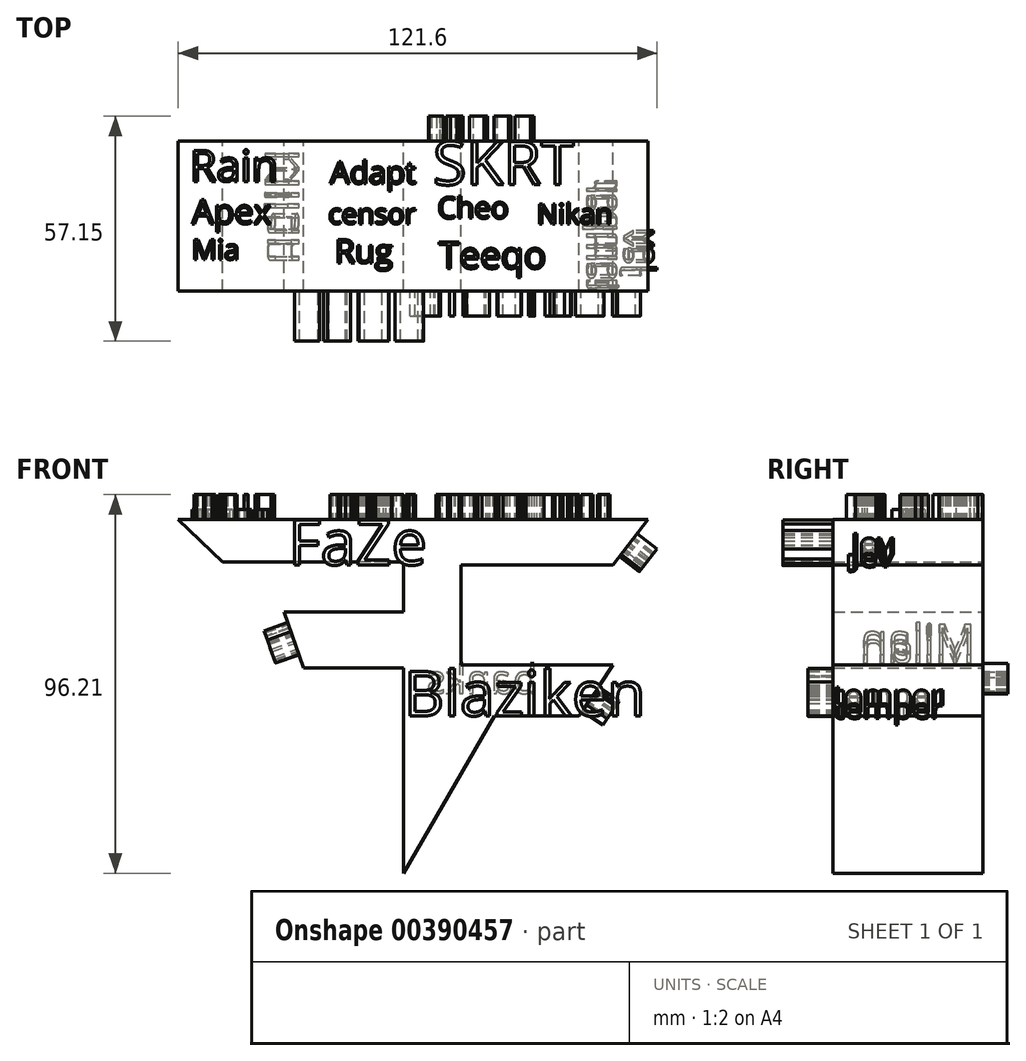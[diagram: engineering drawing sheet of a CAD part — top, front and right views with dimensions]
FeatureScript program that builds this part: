
annotation { "Feature Type Name" : "Feature", "Feature Type Description" : "" }
export const myFeature = defineFeature(function(context is Context, id is Id, definition is map)
    precondition{}
    {
        {
            var Q0;
            Q0=qCreatedBy(makeId("Front.planeOp"),FACE);
            var sketch = newSketch(context, id + "F0", { "sketchPlane" : qUnion([Q0])});
            skLineSegment(sketch, "E0", {"start": v(-52.84, 49.84) * mm, "end": v(58.59, 49.84) * mm});
            skLineSegment(sketch, "E1", {"start": v(58.59, 49.84) * mm, "end": v(49.72, 38.34) * mm});
            skLineSegment(sketch, "E2", {"start": v(49.72, 38.34) * mm, "end": v(11.14, 38.34) * mm});
            skLineSegment(sketch, "E3", {"start": v(11.14, 38.34) * mm, "end": v(11.14, 12.94) * mm});
            skLineSegment(sketch, "E4", {"start": v(11.14, 12.94) * mm, "end": v(49.72, 12.94) * mm});
            skLineSegment(sketch, "E5", {"start": v(49.72, 12.94) * mm, "end": v(41.1, 0) * mm});
            skLineSegment(sketch, "E6", {"start": v(41.1, 0) * mm, "end": v(19.53, 0) * mm});
            skLineSegment(sketch, "E7", {"start": v(19.53, 0) * mm, "end": v(-3.47, -40.02) * mm});
            skLineSegment(sketch, "E8", {"start": v(-3.47, -40.02) * mm, "end": v(-3.47, 12.22) * mm});
            skLineSegment(sketch, "E9", {"start": v(-3.47, 12.22) * mm, "end": v(-28.87, 12.22) * mm});
            skLineSegment(sketch, "E10", {"start": v(-28.87, 12.22) * mm, "end": v(-33.9, 26.36) * mm});
            skLineSegment(sketch, "E11", {"start": v(-33.9, 26.36) * mm, "end": v(-3.47, 26.36) * mm});
            skLineSegment(sketch, "E12", {"start": v(-3.47, 26.36) * mm, "end": v(-3.47, 39.06) * mm});
            skLineSegment(sketch, "E13", {"start": v(-3.47, 39.06) * mm, "end": v(-49.48, 39.06) * mm});
            skLineSegment(sketch, "E14", {"start": v(-49.48, 39.06) * mm, "end": v(-60.74, 49.84) * mm});
            skLineSegment(sketch, "E15", {"start": v(-60.74, 49.84) * mm, "end": v(-52.84, 49.84) * mm});
            skSolve(sketch);
        }
        {
            var Q0;
            Q0 = qSketchRegion(id + "F0", true);
            extrude(context, id + "F1", {"entities" : qUnion([Q0]), "depth" : 38.1 * mm});
        }
        {
            var Q0;
            Q0 = qSketchRegion(id + "F0", true);
            extrude(context, id + "F2", {"entities" : qUnion([Q0]), "operationType" : NewBodyOperationType.ADD, "depth" : 25.4 * mm});
        }
        {
            var Q0;
            Q0=makeQuery(id+"F1.opExtrude","CAP_FACE",FACE,{"disambiguationData":[OSD([sQuery(id+"F0.wireOp",EDGE,"E0"),sQuery(id+"F0.wireOp",EDGE,"E1"),sQuery(id+"F0.wireOp",EDGE,"E2"),sQuery(id+"F0.wireOp",EDGE,"E3"),sQuery(id+"F0.wireOp",EDGE,"E4"),sQuery(id+"F0.wireOp",EDGE,"E5"),sQuery(id+"F0.wireOp",EDGE,"E6"),sQuery(id+"F0.wireOp",EDGE,"E7"),sQuery(id+"F0.wireOp",EDGE,"E8"),sQuery(id+"F0.wireOp",EDGE,"E9"),sQuery(id+"F0.wireOp",EDGE,"E10"),sQuery(id+"F0.wireOp",EDGE,"E11"),sQuery(id+"F0.wireOp",EDGE,"E12"),sQuery(id+"F0.wireOp",EDGE,"E13"),sQuery(id+"F0.wireOp",EDGE,"E14"),sQuery(id+"F0.wireOp",EDGE,"E15")])],"isStart":false});
            var sketch = newSketch(context, id + "F3", { "sketchPlane" : qUnion([Q0])});
            skText(sketch, "E16", { "text": "FaZe", "fontName": "OpenSans-Regular.ttf"});
            const initialGuessF3  = {"E16": [-0.03281, 0.03834, 1, 0, 0.0115]};
            skSetInitialGuess(sketch, initialGuessF3);
            skSolve(sketch);
        }
        {
            var Q0;
            Q0 = qSketchRegion(id + "F3", true);
            extrude(context, id + "F4", {"entities" : qUnion([Q0]), "operationType" : NewBodyOperationType.ADD, "depth" : 12.7 * mm});
        }
        {
            var Q0;
            Q0=makeQuery(id+"F1.opExtrude","SWEPT_FACE",FACE,{"disambiguationData":[OSD([sQuery(id+"F0.wireOp",EDGE,"E0"),sQuery(id+"F0.wireOp",EDGE,"E15")])]});
            var sketch = newSketch(context, id + "F5", { "sketchPlane" : qUnion([Q0])});
            skText(sketch, "E17", { "text": "Rain", "fontName": "OpenSans-Regular.ttf"});
            const initialGuessF5  = {"E17": [-0.05788, -0.01021, 1, 0, 0.00794]};
            skSetInitialGuess(sketch, initialGuessF5);
            skSolve(sketch);
        }
        {
            var Q0;
            Q0 = qSketchRegion(id + "F5", true);
            extrude(context, id + "F6", {"entities" : qUnion([Q0]), "operationType" : NewBodyOperationType.ADD, "depth" : 6.35 * mm});
        }
        {
            var Q0;
            {var subQ0=sQuery(id+"F0.wireOp",EDGE,"E1");var subQ1=sQuery(id+"F0.wireOp",EDGE,"E15");var subQ15=sQuery(id+"F0.wireOp",EDGE,"E0");Q0=makeQuery(id+"F6.boolean.opBoolean","SPLIT",FACE,{"disambiguationData":[TD([makeQuery(id+"F1.opExtrude","SWEPT_FACE",FACE,{"disambiguationData":[OSD([subQ0])]})])],"derivedFrom":makeQuery(id+"F1.opExtrude","SWEPT_FACE",FACE,{"disambiguationData":[OSD([subQ15,subQ1])]})});}
            var sketch = newSketch(context, id + "F7", { "sketchPlane" : qUnion([Q0])});
            skText(sketch, "E18", { "text": "Apex", "fontName": "OpenSans-Regular.ttf"});
            const initialGuessF7  = {"E18": [-0.05731, -0.021, 1, 0, 0.00624]};
            skSetInitialGuess(sketch, initialGuessF7);
            skSolve(sketch);
        }
        {
            var Q0;
            Q0 = qSketchRegion(id + "F7", true);
            extrude(context, id + "F8", {"entities" : qUnion([Q0]), "operationType" : NewBodyOperationType.ADD, "depth" : 2.54 * mm});
        }
        {
            var Q0;
            {var subQ52=sQuery(id+"F0.wireOp",EDGE,"E15");var subQ65=sQuery(id+"F0.wireOp",EDGE,"E1");var subQ66=sQuery(id+"F0.wireOp",EDGE,"E0");var subQ72=makeQuery(id+"F1.opExtrude","SWEPT_FACE",FACE,{"disambiguationData":[OSD([subQ65])]});Q0=makeQuery(id+"F8.boolean.opBoolean","SPLIT",FACE,{"disambiguationData":[TD([subQ72])],"derivedFrom":makeQuery(id+"F6.boolean.opBoolean","SPLIT",FACE,{"disambiguationData":[TD([subQ72])],"derivedFrom":makeQuery(id+"F1.opExtrude","SWEPT_FACE",FACE,{"disambiguationData":[OSD([subQ66,subQ52])]})})});}
            var sketch = newSketch(context, id + "F9", { "sketchPlane" : qUnion([Q0])});
            skText(sketch, "E19", { "text": "Adapt", "fontName": "OpenSans-Regular.ttf"});
            const initialGuessF9  = {"E19": [-0.02216, -0.01078, 1, 0, 0.00567]};
            skSetInitialGuess(sketch, initialGuessF9);
            skSolve(sketch);
        }
        {
            var Q0;
            Q0 = qSketchRegion(id + "F9", true);
            extrude(context, id + "F10", {"entities" : qUnion([Q0]), "operationType" : NewBodyOperationType.ADD, "depth" : 6.35 * mm});
        }
        {
            var Q0;
            {var subQ81=sQuery(id+"F0.wireOp",EDGE,"E15");var subQ94=sQuery(id+"F0.wireOp",EDGE,"E1");var subQ95=sQuery(id+"F0.wireOp",EDGE,"E0");var subQ103=makeQuery(id+"F1.opExtrude","SWEPT_FACE",FACE,{"disambiguationData":[OSD([subQ94])]});Q0=makeQuery(id+"F10.boolean.opBoolean","SPLIT",FACE,{"disambiguationData":[TD([subQ103])],"derivedFrom":makeQuery(id+"F8.boolean.opBoolean","SPLIT",FACE,{"disambiguationData":[TD([subQ103])],"derivedFrom":makeQuery(id+"F6.boolean.opBoolean","SPLIT",FACE,{"disambiguationData":[TD([subQ103])],"derivedFrom":makeQuery(id+"F1.opExtrude","SWEPT_FACE",FACE,{"disambiguationData":[OSD([subQ95,subQ81])]})})})});}
            var sketch = newSketch(context, id + "F11", { "sketchPlane" : qUnion([Q0])});
            skText(sketch, "E20", { "text": "censor", "fontName": "OpenSans-Regular.ttf"});
            const initialGuessF11  = {"E20": [-0.02263, -0.021, 1, 0, 0.0051]};
            skSetInitialGuess(sketch, initialGuessF11);
            skSolve(sketch);
        }
        {
            var Q0;
            Q0 = qSketchRegion(id + "F11", true);
            extrude(context, id + "F12", {"entities" : qUnion([Q0]), "operationType" : NewBodyOperationType.ADD, "depth" : 6.35 * mm});
        }
        {
            var Q0;
            {var subQ25=sQuery(id+"F0.wireOp",EDGE,"E9");var subQ27=sQuery(id+"F0.wireOp",EDGE,"E8");var subQ29=sQuery(id+"F0.wireOp",EDGE,"E7");var subQ31=sQuery(id+"F0.wireOp",EDGE,"E6");var subQ33=sQuery(id+"F0.wireOp",EDGE,"E5");var subQ35=sQuery(id+"F0.wireOp",EDGE,"E4");var subQ37=sQuery(id+"F0.wireOp",EDGE,"E15");var subQ38=sQuery(id+"F0.wireOp",EDGE,"E0");var subQ41=sQuery(id+"F0.wireOp",EDGE,"E1");var subQ43=sQuery(id+"F0.wireOp",EDGE,"E2");var subQ45=sQuery(id+"F0.wireOp",EDGE,"E3");var subQ47=sQuery(id+"F0.wireOp",EDGE,"E10");var subQ49=sQuery(id+"F0.wireOp",EDGE,"E11");var subQ51=sQuery(id+"F0.wireOp",EDGE,"E12");var subQ52=sQuery(id+"F0.wireOp",EDGE,"E13");var subQ53=sQuery(id+"F0.wireOp",EDGE,"E14");Q0=makeQuery(id+"F4.boolean.opBoolean","SPLIT",FACE,{"disambiguationData":[TD([makeQuery(id+"F1.opExtrude","SWEPT_FACE",FACE,{"disambiguationData":[OSD([subQ41])]})])],"derivedFrom":makeQuery(id+"F1.opExtrude","CAP_FACE",FACE,{"disambiguationData":[OSD([subQ38,subQ41,subQ43,subQ45,subQ35,subQ33,subQ31,subQ29,subQ27,subQ25,subQ47,subQ49,subQ51,subQ52,subQ53,subQ37])],"isStart":false})});}
            var sketch = newSketch(context, id + "F13", { "sketchPlane" : qUnion([Q0])});
            skText(sketch, "E21", { "text": "Blaziken", "fontName": "OpenSans-Regular.ttf"});
            skPoint(sketch, "E21.secondSnap0", {"position": v(30.31, 0) * mm});
            const initialGuessF13  = {"E21": [-0.00347, 0, 1, 0, 0.0114]};
            skSetInitialGuess(sketch, initialGuessF13);
            skSolve(sketch);
        }
        {
            var Q0;
            Q0 = qSketchRegion(id + "F13", true);
            extrude(context, id + "F14", {"entities" : qUnion([Q0]), "operationType" : NewBodyOperationType.ADD, "depth" : 6.35 * mm});
        }
        {
            var Q0;
            {var subQ109=sQuery(id+"F0.wireOp",EDGE,"E1");var subQ110=makeQuery(id+"F1.opExtrude","SWEPT_FACE",FACE,{"disambiguationData":[OSD([subQ109])]});var subQ114=sQuery(id+"F0.wireOp",EDGE,"E15");var subQ128=sQuery(id+"F0.wireOp",EDGE,"E0");Q0=makeQuery(id+"F12.boolean.opBoolean","SPLIT",FACE,{"disambiguationData":[TD([subQ110])],"derivedFrom":makeQuery(id+"F10.boolean.opBoolean","SPLIT",FACE,{"disambiguationData":[TD([subQ110])],"derivedFrom":makeQuery(id+"F8.boolean.opBoolean","SPLIT",FACE,{"disambiguationData":[TD([subQ110])],"derivedFrom":makeQuery(id+"F6.boolean.opBoolean","SPLIT",FACE,{"disambiguationData":[TD([subQ110])],"derivedFrom":makeQuery(id+"F1.opExtrude","SWEPT_FACE",FACE,{"disambiguationData":[OSD([subQ128,subQ114])]})})})})});}
            var sketch = newSketch(context, id + "F15", { "sketchPlane" : qUnion([Q0])});
            skText(sketch, "E22", { "text": "SKRT", "fontName": "OpenSans-Regular.ttf"});
            const initialGuessF15  = {"E22": [0.00397, -0.01107, 1, 0, 0.01107]};
            skSetInitialGuess(sketch, initialGuessF15);
            skSolve(sketch);
        }
        {
            var Q0;
            Q0 = qSketchRegion(id + "F15", true);
            extrude(context, id + "F16", {"entities" : qUnion([Q0]), "operationType" : NewBodyOperationType.ADD, "depth" : 6.35 * mm});
        }
        {
            var Q0;
            {var subQ126=sQuery(id+"F0.wireOp",EDGE,"E1");var subQ127=makeQuery(id+"F1.opExtrude","SWEPT_FACE",FACE,{"disambiguationData":[OSD([subQ126])]});var subQ131=sQuery(id+"F0.wireOp",EDGE,"E15");var subQ145=sQuery(id+"F0.wireOp",EDGE,"E0");Q0=makeQuery(id+"F16.boolean.opBoolean","SPLIT",FACE,{"disambiguationData":[TD([subQ127])],"derivedFrom":makeQuery(id+"F12.boolean.opBoolean","SPLIT",FACE,{"disambiguationData":[TD([subQ127])],"derivedFrom":makeQuery(id+"F10.boolean.opBoolean","SPLIT",FACE,{"disambiguationData":[TD([subQ127])],"derivedFrom":makeQuery(id+"F8.boolean.opBoolean","SPLIT",FACE,{"disambiguationData":[TD([subQ127])],"derivedFrom":makeQuery(id+"F6.boolean.opBoolean","SPLIT",FACE,{"disambiguationData":[TD([subQ127])],"derivedFrom":makeQuery(id+"F1.opExtrude","SWEPT_FACE",FACE,{"disambiguationData":[OSD([subQ145,subQ131])]})})})})})});}
            var sketch = newSketch(context, id + "F17", { "sketchPlane" : qUnion([Q0])});
            skText(sketch, "E23", { "text": "Cheo", "fontName": "OpenSans-Regular.ttf"});
            const initialGuessF17  = {"E23": [0.0051, -0.01958, 1, 0, 0.0054]};
            skSetInitialGuess(sketch, initialGuessF17);
            skSolve(sketch);
        }
        {
            var Q0;
            Q0 = qSketchRegion(id + "F17", true);
            extrude(context, id + "F18", {"entities" : qUnion([Q0]), "operationType" : NewBodyOperationType.ADD, "depth" : 6.35 * mm});
        }
        {
            var Q0;
            {var subQ127=sQuery(id+"F0.wireOp",EDGE,"E1");var subQ128=makeQuery(id+"F1.opExtrude","SWEPT_FACE",FACE,{"disambiguationData":[OSD([subQ127])]});var subQ132=sQuery(id+"F0.wireOp",EDGE,"E15");var subQ146=sQuery(id+"F0.wireOp",EDGE,"E0");Q0=makeQuery(id+"F18.boolean.opBoolean","SPLIT",FACE,{"disambiguationData":[TD([subQ128])],"derivedFrom":makeQuery(id+"F16.boolean.opBoolean","SPLIT",FACE,{"disambiguationData":[TD([subQ128])],"derivedFrom":makeQuery(id+"F12.boolean.opBoolean","SPLIT",FACE,{"disambiguationData":[TD([subQ128])],"derivedFrom":makeQuery(id+"F10.boolean.opBoolean","SPLIT",FACE,{"disambiguationData":[TD([subQ128])],"derivedFrom":makeQuery(id+"F8.boolean.opBoolean","SPLIT",FACE,{"disambiguationData":[TD([subQ128])],"derivedFrom":makeQuery(id+"F6.boolean.opBoolean","SPLIT",FACE,{"disambiguationData":[TD([subQ128])],"derivedFrom":makeQuery(id+"F1.opExtrude","SWEPT_FACE",FACE,{"disambiguationData":[OSD([subQ146,subQ132])]})})})})})})});}
            var sketch = newSketch(context, id + "F19", { "sketchPlane" : qUnion([Q0])});
            skText(sketch, "E24", { "text": "Mia", "fontName": "OpenSans-Regular.ttf"});
            const initialGuessF19  = {"E24": [-0.05731, -0.03007, 1, 0, 0.0051]};
            skSetInitialGuess(sketch, initialGuessF19);
            skSolve(sketch);
        }
        {
            var Q0;
            Q0 = qSketchRegion(id + "F19", true);
            extrude(context, id + "F20", {"entities" : qUnion([Q0]), "operationType" : NewBodyOperationType.ADD, "depth" : 6.35 * mm});
        }
        {
            var Q0;
            {var subQ222=sQuery(id+"F0.wireOp",EDGE,"E15");var subQ236=sQuery(id+"F0.wireOp",EDGE,"E1");var subQ237=sQuery(id+"F0.wireOp",EDGE,"E0");var subQ296=makeQuery(id+"F1.opExtrude","SWEPT_FACE",FACE,{"disambiguationData":[OSD([subQ236])]});Q0=makeQuery(id+"F20.boolean.opBoolean","SPLIT",FACE,{"disambiguationData":[TD([subQ296])],"derivedFrom":makeQuery(id+"F18.boolean.opBoolean","SPLIT",FACE,{"disambiguationData":[TD([subQ296])],"derivedFrom":makeQuery(id+"F16.boolean.opBoolean","SPLIT",FACE,{"disambiguationData":[TD([subQ296])],"derivedFrom":makeQuery(id+"F12.boolean.opBoolean","SPLIT",FACE,{"disambiguationData":[TD([subQ296])],"derivedFrom":makeQuery(id+"F10.boolean.opBoolean","SPLIT",FACE,{"disambiguationData":[TD([subQ296])],"derivedFrom":makeQuery(id+"F8.boolean.opBoolean","SPLIT",FACE,{"disambiguationData":[TD([subQ296])],"derivedFrom":makeQuery(id+"F6.boolean.opBoolean","SPLIT",FACE,{"disambiguationData":[TD([subQ296])],"derivedFrom":makeQuery(id+"F1.opExtrude","SWEPT_FACE",FACE,{"disambiguationData":[OSD([subQ237,subQ222])]})})})})})})})});}
            var sketch = newSketch(context, id + "F21", { "sketchPlane" : qUnion([Q0])});
            skText(sketch, "E25", { "text": "Rug", "fontName": "OpenSans-Regular.ttf"});
            const initialGuessF21  = {"E25": [-0.021, -0.03093, 1, 0, 0.00596]};
            skSetInitialGuess(sketch, initialGuessF21);
            skSolve(sketch);
        }
        {
            var Q0;
            Q0 = qSketchRegion(id + "F21", true);
            extrude(context, id + "F22", {"entities" : qUnion([Q0]), "operationType" : NewBodyOperationType.ADD, "depth" : 6.35 * mm});
        }
        {
            var Q0;
            {var subQ228=sQuery(id+"F0.wireOp",EDGE,"E15");var subQ242=sQuery(id+"F0.wireOp",EDGE,"E1");var subQ243=sQuery(id+"F0.wireOp",EDGE,"E0");var subQ302=makeQuery(id+"F1.opExtrude","SWEPT_FACE",FACE,{"disambiguationData":[OSD([subQ242])]});Q0=makeQuery(id+"F22.boolean.opBoolean","SPLIT",FACE,{"disambiguationData":[TD([subQ302])],"derivedFrom":makeQuery(id+"F20.boolean.opBoolean","SPLIT",FACE,{"disambiguationData":[TD([subQ302])],"derivedFrom":makeQuery(id+"F18.boolean.opBoolean","SPLIT",FACE,{"disambiguationData":[TD([subQ302])],"derivedFrom":makeQuery(id+"F16.boolean.opBoolean","SPLIT",FACE,{"disambiguationData":[TD([subQ302])],"derivedFrom":makeQuery(id+"F12.boolean.opBoolean","SPLIT",FACE,{"disambiguationData":[TD([subQ302])],"derivedFrom":makeQuery(id+"F10.boolean.opBoolean","SPLIT",FACE,{"disambiguationData":[TD([subQ302])],"derivedFrom":makeQuery(id+"F8.boolean.opBoolean","SPLIT",FACE,{"disambiguationData":[TD([subQ302])],"derivedFrom":makeQuery(id+"F6.boolean.opBoolean","SPLIT",FACE,{"disambiguationData":[TD([subQ302])],"derivedFrom":makeQuery(id+"F1.opExtrude","SWEPT_FACE",FACE,{"disambiguationData":[OSD([subQ243,subQ228])]})})})})})})})})});}
            var sketch = newSketch(context, id + "F23", { "sketchPlane" : qUnion([Q0])});
            skText(sketch, "E26", { "text": "Teeqo", "fontName": "OpenSans-Regular.ttf"});
            const initialGuessF23  = {"E26": [0.0054, -0.03234, 1, 0, 0.0068]};
            skSetInitialGuess(sketch, initialGuessF23);
            skSolve(sketch);
        }
        {
            var Q0;
            Q0 = qSketchRegion(id + "F23", true);
            extrude(context, id + "F24", {"entities" : qUnion([Q0]), "operationType" : NewBodyOperationType.ADD, "depth" : 6.35 * mm});
        }
        {
            var Q0;
            {var subQ239=sQuery(id+"F0.wireOp",EDGE,"E15");var subQ253=sQuery(id+"F0.wireOp",EDGE,"E1");var subQ254=sQuery(id+"F0.wireOp",EDGE,"E0");var subQ317=makeQuery(id+"F1.opExtrude","SWEPT_FACE",FACE,{"disambiguationData":[OSD([subQ253])]});Q0=makeQuery(id+"F24.boolean.opBoolean","SPLIT",FACE,{"disambiguationData":[TD([subQ317])],"derivedFrom":makeQuery(id+"F22.boolean.opBoolean","SPLIT",FACE,{"disambiguationData":[TD([subQ317])],"derivedFrom":makeQuery(id+"F20.boolean.opBoolean","SPLIT",FACE,{"disambiguationData":[TD([subQ317])],"derivedFrom":makeQuery(id+"F18.boolean.opBoolean","SPLIT",FACE,{"disambiguationData":[TD([subQ317])],"derivedFrom":makeQuery(id+"F16.boolean.opBoolean","SPLIT",FACE,{"disambiguationData":[TD([subQ317])],"derivedFrom":makeQuery(id+"F12.boolean.opBoolean","SPLIT",FACE,{"disambiguationData":[TD([subQ317])],"derivedFrom":makeQuery(id+"F10.boolean.opBoolean","SPLIT",FACE,{"disambiguationData":[TD([subQ317])],"derivedFrom":makeQuery(id+"F8.boolean.opBoolean","SPLIT",FACE,{"disambiguationData":[TD([subQ317])],"derivedFrom":makeQuery(id+"F6.boolean.opBoolean","SPLIT",FACE,{"disambiguationData":[TD([subQ317])],"derivedFrom":makeQuery(id+"F1.opExtrude","SWEPT_FACE",FACE,{"disambiguationData":[OSD([subQ254,subQ239])]})})})})})})})})})});}
            var sketch = newSketch(context, id + "F25", { "sketchPlane" : qUnion([Q0])});
            skText(sketch, "E27", { "text": "Nikan", "fontName": "OpenSans-Regular.ttf"});
            const initialGuessF25  = {"E27": [0.03036, -0.021, 1, 0, 0.0051]};
            skSetInitialGuess(sketch, initialGuessF25);
            skSolve(sketch);
        }
        {
            var Q0;
            Q0 = qSketchRegion(id + "F25", true);
            extrude(context, id + "F26", {"entities" : qUnion([Q0]), "operationType" : NewBodyOperationType.ADD, "depth" : 6.35 * mm});
        }
        {
            var Q0;
            Q0=makeQuery(id+"F1.opExtrude","CAP_FACE",FACE,{"disambiguationData":[OSD([sQuery(id+"F0.wireOp",EDGE,"E0"),sQuery(id+"F0.wireOp",EDGE,"E1"),sQuery(id+"F0.wireOp",EDGE,"E2"),sQuery(id+"F0.wireOp",EDGE,"E3"),sQuery(id+"F0.wireOp",EDGE,"E4"),sQuery(id+"F0.wireOp",EDGE,"E5"),sQuery(id+"F0.wireOp",EDGE,"E6"),sQuery(id+"F0.wireOp",EDGE,"E7"),sQuery(id+"F0.wireOp",EDGE,"E8"),sQuery(id+"F0.wireOp",EDGE,"E9"),sQuery(id+"F0.wireOp",EDGE,"E10"),sQuery(id+"F0.wireOp",EDGE,"E11"),sQuery(id+"F0.wireOp",EDGE,"E12"),sQuery(id+"F0.wireOp",EDGE,"E13"),sQuery(id+"F0.wireOp",EDGE,"E14"),sQuery(id+"F0.wireOp",EDGE,"E15")])],"isStart":true});
            var sketch = newSketch(context, id + "F27", { "sketchPlane" : qUnion([Q0])});
            skText(sketch, "E28", { "text": "banks\n", "fontName": "OpenSans-Regular.ttf"});
            const initialGuessF27  = {"E28": [-0.03043, 0.00567, 1, 0, 0.00727]};
            skSetInitialGuess(sketch, initialGuessF27);
            skSolve(sketch);
        }
        {
            var Q0;
            Q0 = qSketchRegion(id + "F27", true);
            extrude(context, id + "F28", {"entities" : qUnion([Q0]), "operationType" : NewBodyOperationType.ADD, "depth" : 6.35 * mm});
        }
        {
            var Q0;
            Q0=makeQuery(id+"F1.opExtrude","SWEPT_FACE",FACE,{"disambiguationData":[OSD([sQuery(id+"F0.wireOp",EDGE,"E10")])]});
            var sketch = newSketch(context, id + "F29", { "sketchPlane" : qUnion([Q0])});
            skText(sketch, "E29", { "text": "Milan", "fontName": "OpenSans-Regular.ttf"});
            const initialGuessF29  = {"E29": [0.00199, 0.02479, 1, 0, 0.00813]};
            skSetInitialGuess(sketch, initialGuessF29);
            skSolve(sketch);
        }
        {
            var Q0;
            Q0 = qSketchRegion(id + "F29", true);
            extrude(context, id + "F30", {"entities" : qUnion([Q0]), "operationType" : NewBodyOperationType.ADD, "depth" : 6.35 * mm});
        }
        {
            var Q0;
            Q0=makeQuery(id+"F1.opExtrude","SWEPT_FACE",FACE,{"disambiguationData":[OSD([sQuery(id+"F0.wireOp",EDGE,"E5")])]});
            var sketch = newSketch(context, id + "F31", { "sketchPlane" : qUnion([Q0])});
            skText(sketch, "E30", { "text": "temper\n", "fontName": "OpenSans-Regular.ttf"});
            const initialGuessF31  = {"E30": [-0.0381, 0.0262, 1, 0, 0.0059]};
            skSetInitialGuess(sketch, initialGuessF31);
            skSolve(sketch);
        }
        {
            var Q0;
            Q0 = qSketchRegion(id + "F31", true);
            extrude(context, id + "F32", {"entities" : qUnion([Q0]), "operationType" : NewBodyOperationType.ADD, "depth" : 6.35 * mm});
        }
        {
            var Q0;
            Q0=makeQuery(id+"F1.opExtrude","SWEPT_FACE",FACE,{"disambiguationData":[OSD([sQuery(id+"F0.wireOp",EDGE,"E1")])]});
            var sketch = newSketch(context, id + "F33", { "sketchPlane" : qUnion([Q0])});
            skText(sketch, "E31", { "text": "Jev\n", "fontName": "OpenSans-Regular.ttf"});
            const initialGuessF33  = {"E31": [-0.03347, 0.06494, 1, 0, 0.00584]};
            skSetInitialGuess(sketch, initialGuessF33);
            skSolve(sketch);
        }
        {
            var Q0;
            Q0 = qSketchRegion(id + "F33", true);
            extrude(context, id + "F34", {"entities" : qUnion([Q0]), "operationType" : NewBodyOperationType.ADD, "depth" : 6.35 * mm});
        }
    });
